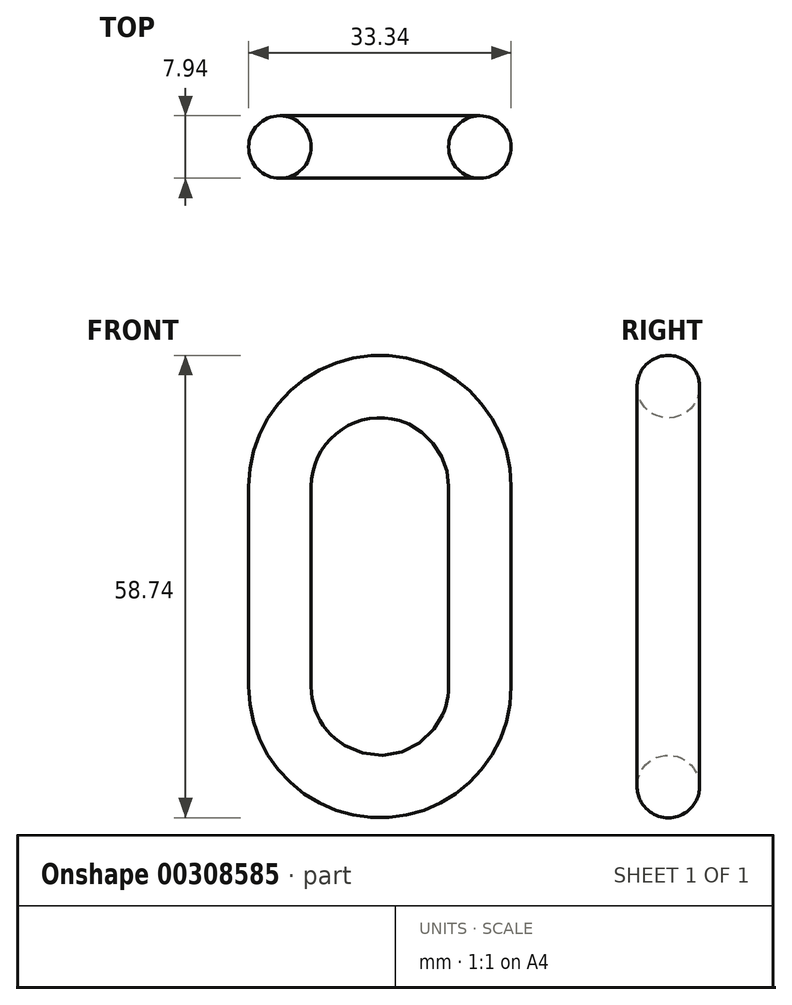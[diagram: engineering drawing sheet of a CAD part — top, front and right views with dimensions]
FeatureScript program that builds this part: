
annotation { "Feature Type Name" : "Feature", "Feature Type Description" : "" }
export const myFeature = defineFeature(function(context is Context, id is Id, definition is map)
    precondition{}
    {
        {
            var Q0;
            Q0=qCreatedBy(makeId("Front.planeOp"),FACE);
            var sketch = newSketch(context, id + "F0", { "sketchPlane" : qUnion([Q0])});
            skLineSegment(sketch, "E0.left", {"start": v(0, 0) * mm, "end": v(0, 25.4) * mm});
            skLineSegment(sketch, "E0.right", {"start": v(-25.4, 0) * mm, "end": v(-25.4, 25.4) * mm});
            skArc(sketch, "E1", {"start": v(-25.4, 0) * mm, "mid": v(-12.7, -12.7) * mm, "end": v(0, 0) * mm});
            skArc(sketch, "E2", {"start": v(0, 25.4) * mm, "mid": v(-12.7, 38.1) * mm, "end": v(-25.4, 25.4) * mm});
            skSolve(sketch);
        }
        {
            var Q0;
            Q0=qCreatedBy(makeId("Top.planeOp"),FACE);
            var sketch = newSketch(context, id + "F1", { "sketchPlane" : qUnion([Q0])});
            skCircle(sketch, "E3", {"center": v(0, 0) * mm, "radius": 3.97 * mm});
            skSolve(sketch);
        }
        {
            var Q0;
            Q0 = qSketchRegion(id + "F1", true);
            var Q1;
            Q1 = qConstructionFilter(qBodyType(qCreatedBy(id + "F0" ,EDGE), BodyType.WIRE), ConstructionObject.NO);
            sweep(context, id + "F2", {"profiles" : qUnion([Q0]), "path" : qUnion([Q1])});
        }
    });
